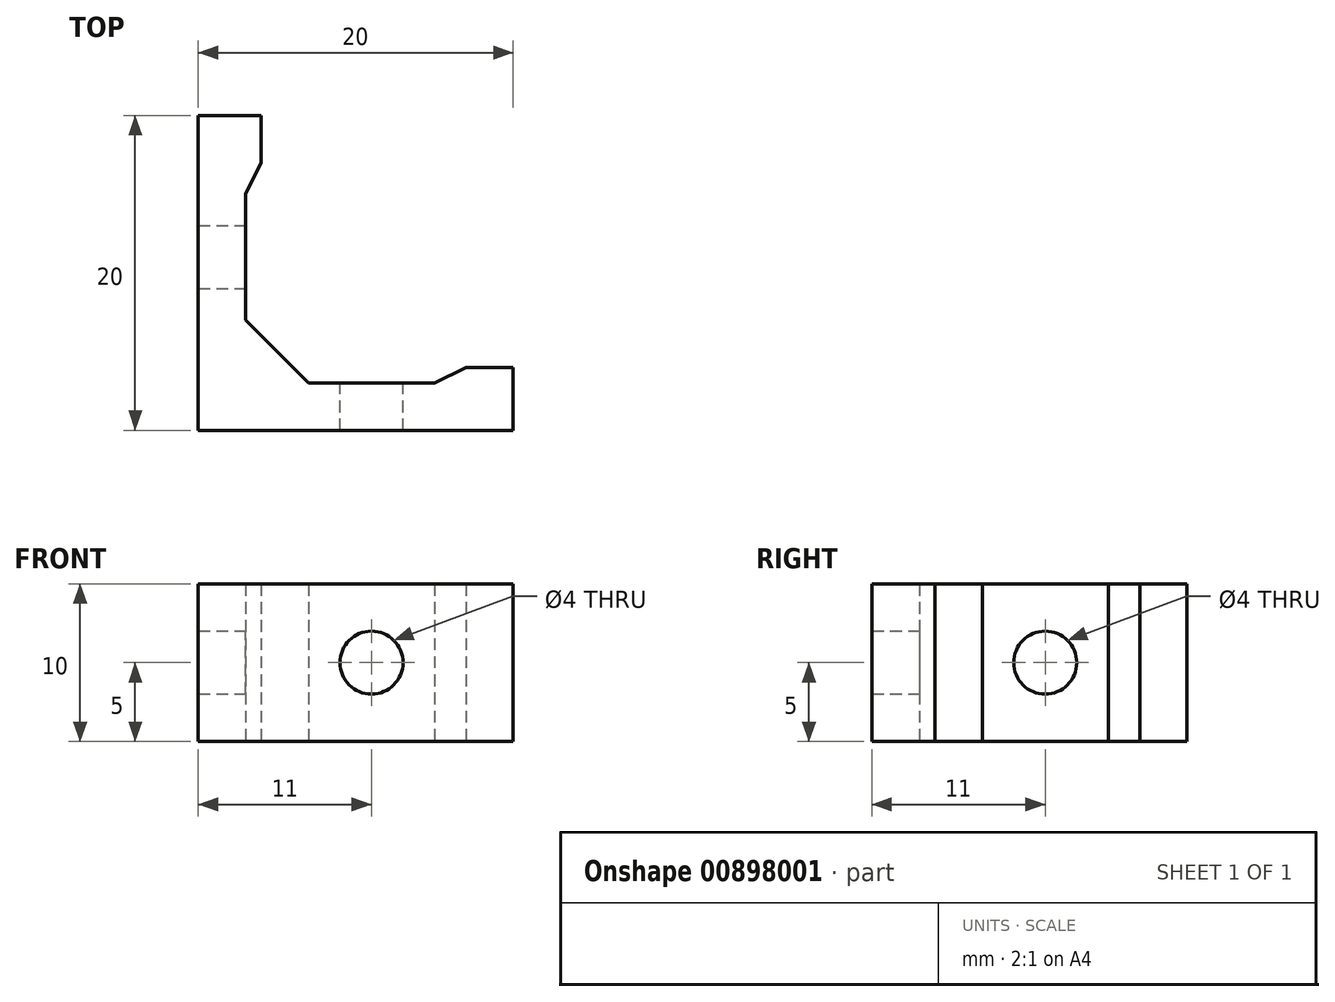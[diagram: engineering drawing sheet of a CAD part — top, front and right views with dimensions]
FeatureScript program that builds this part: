
annotation { "Feature Type Name" : "Feature", "Feature Type Description" : "" }
export const myFeature = defineFeature(function(context is Context, id is Id, definition is map)
    precondition{}
    {
        {
            var Q0;
            Q0=qCreatedBy(makeId("Top.planeOp"),FACE);
            var sketch = newSketch(context, id + "F0", { "sketchPlane" : qUnion([Q0])});
            skLineSegment(sketch, "E0", {"start": v(0, 0) * mm, "end": v(20, 0) * mm});
            skLineSegment(sketch, "E1", {"start": v(0, 0) * mm, "end": v(40, 40) * mm, "construction": true});
            skLineSegment(sketch, "E2", {"start": v(0, 0) * mm, "end": v(0, 40) * mm, "construction": true});
            skLineSegment(sketch, "E3", {"start": v(0, 40) * mm, "end": v(40, 40) * mm, "construction": true});
            skLineSegment(sketch, "E4", {"start": v(40, 40) * mm, "end": v(40, 0) * mm, "construction": true});
            skLineSegment(sketch, "E5", {"start": v(20, 0) * mm, "end": v(20, 4) * mm});
            skLineSegment(sketch, "E6", {"start": v(20, 4) * mm, "end": v(17, 4) * mm});
            skLineSegment(sketch, "E7", {"start": v(17, 4) * mm, "end": v(15, 3) * mm});
            skLineSegment(sketch, "E8", {"start": v(15, 3) * mm, "end": v(7, 3) * mm});
            skLineSegment(sketch, "E9", {"start": v(15, 3) * mm, "end": v(15, 0) * mm, "construction": true});
            skLineSegment(sketch, "E10", {"start": v(15, 3) * mm, "end": v(20, 3) * mm, "construction": true});
            skLineSegment(sketch, "E11", {"start": v(7, 3) * mm, "end": v(5, 5) * mm});
            skLineSegment(sketch, "E12.MirrorCS", {"start": v(3, 7) * mm, "end": v(5, 5) * mm});
            skLineSegment(sketch, "E13.MirrorCS", {"start": v(3, 15) * mm, "end": v(3, 7) * mm});
            skLineSegment(sketch, "E14.MirrorCS", {"start": v(4, 17) * mm, "end": v(3, 15) * mm});
            skLineSegment(sketch, "E15.MirrorCS", {"start": v(4, 20) * mm, "end": v(4, 17) * mm});
            skLineSegment(sketch, "E16.MirrorCS", {"start": v(0, 0) * mm, "end": v(0, 20) * mm});
            skLineSegment(sketch, "E17.MirrorCS", {"start": v(0, 20) * mm, "end": v(4, 20) * mm});
            skSolve(sketch);
        }
        {
            var Q0;
            Q0=makeQuery(id+"F0.imprint","IMPRINT",FACE,{"disambiguationData":[TD([[makeQuery(id+"F0.imprint","IMPRINT",EDGE,{"derivedFrom":sQuery(id+"F0.wireOp",EDGE,"E0")}),1.0]])]});
            extrude(context, id + "F1", {"entities" : qUnion([Q0]), "depth" : 10 * mm, "offsetDistance" : 25 * mm});
        }
        {
            var Q0;
            Q0=makeQuery(id+"F1.opExtrude","SWEPT_FACE",FACE,{"disambiguationData":[OSD([sQuery(id+"F0.wireOp",EDGE,"E13.MirrorCS")])]});
            var sketch = newSketch(context, id + "F2", { "sketchPlane" : qUnion([Q0])});
            skLineSegment(sketch, "E18", {"start": v(0, 0) * mm, "end": v(0, 5) * mm, "construction": true});
            skLineSegment(sketch, "E19", {"start": v(0, 5) * mm, "end": v(11, 5) * mm, "construction": true});
            skCircle(sketch, "E20", {"center": v(11, 5) * mm, "radius": 2 * mm});
            skSolve(sketch);
        }
        {
            var Q0;
            Q0 = qSketchRegion(id + "F2", true);
            extrude(context, id + "F3", {"entities" : qUnion([Q0]), "operationType" : NewBodyOperationType.REMOVE, "oppositeDirection" : true, "depth" : 5 * mm, "offsetDistance" : 25 * mm});
        }
        {
            var Q0;
            Q0=makeQuery(id+"F1.opExtrude","SWEPT_FACE",FACE,{"disambiguationData":[OSD([sQuery(id+"F0.wireOp",EDGE,"E8")])]});
            var sketch = newSketch(context, id + "F4", { "sketchPlane" : qUnion([Q0])});
            skLineSegment(sketch, "E21", {"start": v(0, 0) * mm, "end": v(0, 5) * mm, "construction": true});
            skLineSegment(sketch, "E22", {"start": v(0, 5) * mm, "end": v(-11, 5) * mm, "construction": true});
            skCircle(sketch, "E23", {"center": v(-11, 5) * mm, "radius": 2 * mm});
            skSolve(sketch);
        }
        {
            var Q0;
            Q0 = qSketchRegion(id + "F4", true);
            extrude(context, id + "F5", {"entities" : qUnion([Q0]), "operationType" : NewBodyOperationType.REMOVE, "oppositeDirection" : true, "depth" : 5 * mm, "offsetDistance" : 25 * mm});
        }
    });
